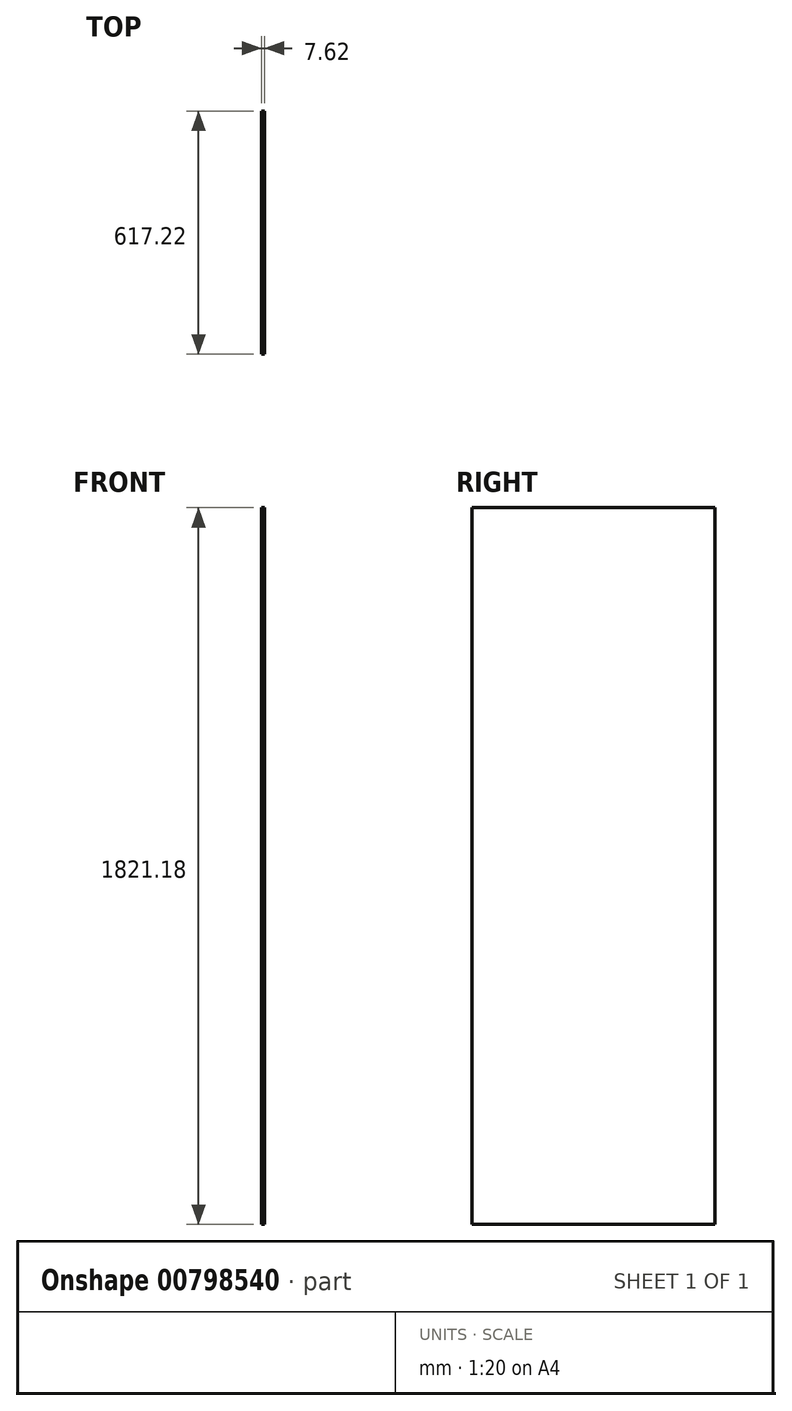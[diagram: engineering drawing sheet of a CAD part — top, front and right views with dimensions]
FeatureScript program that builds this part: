
annotation { "Feature Type Name" : "Feature", "Feature Type Description" : "" }
export const myFeature = defineFeature(function(context is Context, id is Id, definition is map)
    precondition{}
    {
        {
            var Q0;
            Q0=qCreatedBy(makeId("Right.planeOp"),FACE);
            var sketch = newSketch(context, id + "F0", { "sketchPlane" : qUnion([Q0])});
            skLineSegment(sketch, "E0.bottom", {"start": v(-308.6, 910.6) * mm, "end": v(308.61, 910.6) * mm});
            skLineSegment(sketch, "E0.top", {"start": v(-308.61, -910.6) * mm, "end": v(308.6, -910.6) * mm});
            skLineSegment(sketch, "E0.left", {"start": v(-308.6, 910.6) * mm, "end": v(-308.61, -910.6) * mm});
            skLineSegment(sketch, "E0.right", {"start": v(308.61, 910.6) * mm, "end": v(308.6, -910.6) * mm});
            skPoint(sketch, "E0.middle", {"position": v(0, 0) * mm});
            skSolve(sketch);
        }
        {
            var Q0;
            Q0 = qSketchRegion(id + "F0", true);
            extrude(context, id + "F1", {"entities" : qUnion([Q0]), "depth" : 7.62 * mm, "offsetDistance" : 30.48 * mm});
        }
    });
